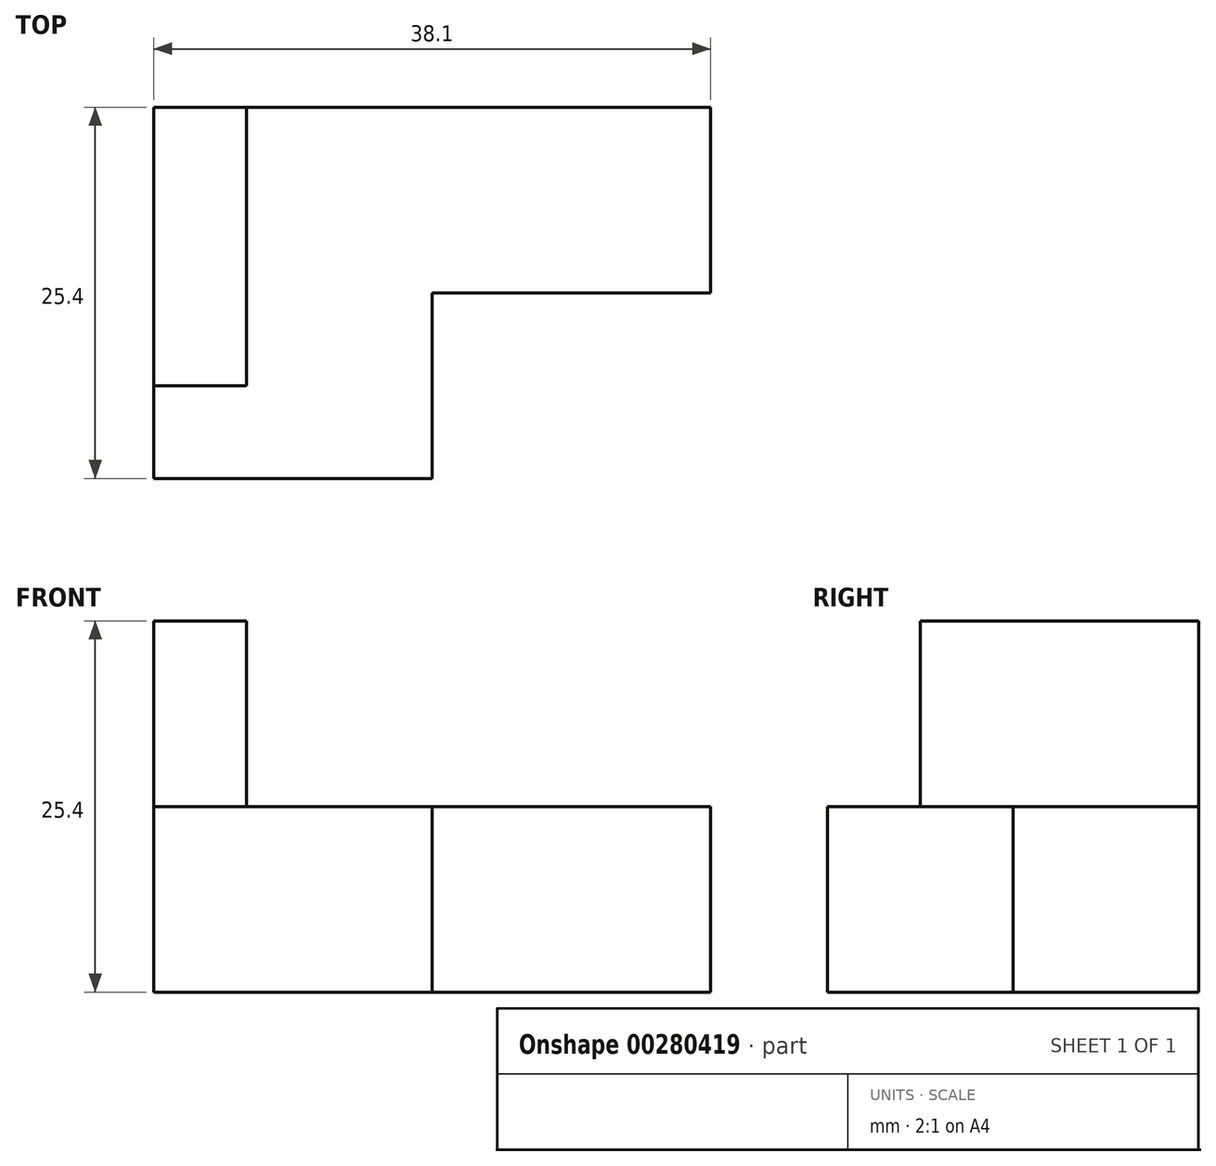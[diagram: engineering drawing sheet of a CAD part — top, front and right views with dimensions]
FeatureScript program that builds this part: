
annotation { "Feature Type Name" : "Feature", "Feature Type Description" : "" }
export const myFeature = defineFeature(function(context is Context, id is Id, definition is map)
    precondition{}
    {
        {
            var Q0;
            Q0=qCreatedBy(makeId("Front.planeOp"),FACE);
            var sketch = newSketch(context, id + "F0", { "sketchPlane" : qUnion([Q0])});
            skLineSegment(sketch, "E0.bottom", {"start": v(0, 0) * mm, "end": v(38.1, 0) * mm});
            skLineSegment(sketch, "E0.top", {"start": v(0, 12.7) * mm, "end": v(38.1, 12.7) * mm});
            skLineSegment(sketch, "E0.left", {"start": v(0, 0) * mm, "end": v(0, 12.7) * mm});
            skLineSegment(sketch, "E0.right", {"start": v(38.1, 0) * mm, "end": v(38.1, 12.7) * mm});
            skLineSegment(sketch, "E1", {"start": v(0, 12.7) * mm, "end": v(0, 25.4) * mm});
            skLineSegment(sketch, "E2", {"start": v(0, 25.4) * mm, "end": v(6.35, 25.4) * mm});
            skLineSegment(sketch, "E3", {"start": v(6.35, 25.4) * mm, "end": v(6.35, 12.7) * mm});
            skSolve(sketch);
        }
        {
            var Q0;
            Q0 = qSketchRegion(id + "F0", true);
            extrude(context, id + "F1", {"entities" : qUnion([Q0]), "depth" : 25.4 * mm, "symmetric" : true});
        }
        {
            var Q0;
            Q0=makeQuery(id+"F1.opExtrude","SWEPT_FACE",FACE,{"disambiguationData":[OSD([sQuery(id+"F0.wireOp",EDGE,"E0.right")])]});
            var sketch = newSketch(context, id + "F2", { "sketchPlane" : qUnion([Q0])});
            skLineSegment(sketch, "E4", {"start": v(0, 0) * mm, "end": v(0, 12.7) * mm});
            skLineSegment(sketch, "E5", {"start": v(0, 12.7) * mm, "end": v(-12.7, 12.7) * mm});
            skLineSegment(sketch, "E6", {"start": v(-12.7, 12.7) * mm, "end": v(-12.7, 0) * mm});
            skLineSegment(sketch, "E7", {"start": v(-12.7, 0) * mm, "end": v(0, 0) * mm});
            skSolve(sketch);
        }
        {
            var Q0;
            Q0=makeQuery(id+"F2.imprint","IMPRINT",FACE,{"disambiguationData":[TD([[makeQuery(id+"F2.imprint","IMPRINT",EDGE,{"derivedFrom":sQuery(id+"F2.wireOp",EDGE,"E4")}),1.0]])]});
            extrude(context, id + "F3", {"entities" : qUnion([Q0]), "operationType" : NewBodyOperationType.REMOVE, "oppositeDirection" : true, "depth" : 19.05 * mm});
        }
        {
            var Q0;
            Q0=makeQuery(id+"F1.opExtrude","CAP_FACE",FACE,{"disambiguationData":[OSD([sQuery(id+"F0.wireOp",EDGE,"E0.bottom"),sQuery(id+"F0.wireOp",EDGE,"E0.top"),sQuery(id+"F0.wireOp",EDGE,"E0.left"),sQuery(id+"F0.wireOp",EDGE,"E0.right"),sQuery(id+"F0.wireOp",EDGE,"E1"),sQuery(id+"F0.wireOp",EDGE,"E2"),sQuery(id+"F0.wireOp",EDGE,"E3")])],"isStart":false});
            var sketch = newSketch(context, id + "F4", { "sketchPlane" : qUnion([Q0])});
            skLineSegment(sketch, "E8", {"start": v(6.35, 12.7) * mm, "end": v(0, 12.7) * mm});
            skLineSegment(sketch, "E9", {"start": v(0, 12.7) * mm, "end": v(0, 25.4) * mm});
            skLineSegment(sketch, "E10", {"start": v(0, 25.4) * mm, "end": v(6.35, 25.4) * mm});
            skLineSegment(sketch, "E11", {"start": v(6.35, 25.4) * mm, "end": v(6.35, 12.7) * mm});
            skSolve(sketch);
        }
        {
            var Q0;
            Q0 = qSketchRegion(id + "F4", true);
            extrude(context, id + "F5", {"entities" : qUnion([Q0]), "operationType" : NewBodyOperationType.REMOVE, "oppositeDirection" : true, "depth" : 6.35 * mm});
        }
    });
